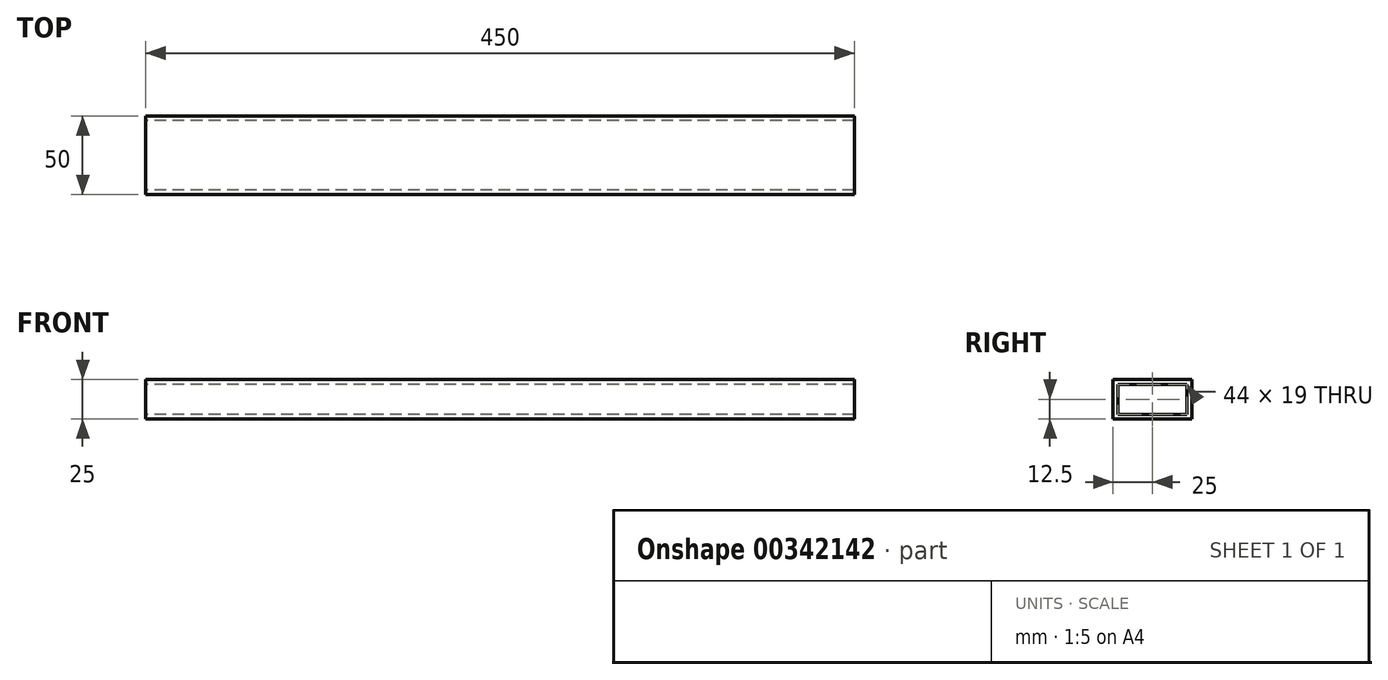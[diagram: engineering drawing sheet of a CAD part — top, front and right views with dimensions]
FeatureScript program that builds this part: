
annotation { "Feature Type Name" : "Feature", "Feature Type Description" : "" }
export const myFeature = defineFeature(function(context is Context, id is Id, definition is map)
    precondition{}
    {
        {
            var Q0;
            Q0=qCreatedBy(makeId("Right.planeOp"),FACE);
            var sketch = newSketch(context, id + "F0", { "sketchPlane" : qUnion([Q0])});
            skLineSegment(sketch, "E0.bottom", {"start": v(-25, 12.5) * mm, "end": v(25, 12.5) * mm});
            skLineSegment(sketch, "E0.top", {"start": v(-25, -12.5) * mm, "end": v(25, -12.5) * mm});
            skLineSegment(sketch, "E0.left", {"start": v(-25, 12.5) * mm, "end": v(-25, -12.5) * mm});
            skLineSegment(sketch, "E0.right", {"start": v(25, 12.5) * mm, "end": v(25, -12.5) * mm});
            skPoint(sketch, "E0.middle", {"position": v(0, 0) * mm});
            skLineSegment(sketch, "E1.bottom", {"start": v(-22, 9.5) * mm, "end": v(22, 9.5) * mm});
            skLineSegment(sketch, "E1.top", {"start": v(-22, -9.5) * mm, "end": v(22, -9.5) * mm});
            skLineSegment(sketch, "E1.left", {"start": v(-22, 9.5) * mm, "end": v(-22, -9.5) * mm});
            skLineSegment(sketch, "E1.right", {"start": v(22, 9.5) * mm, "end": v(22, -9.5) * mm});
            skSolve(sketch);
        }
        {
            var Q0;
            Q0=qSketchRegion(id+"F0",true);
            extrude(context, id + "F1", {"entities" : qUnion([Q0]), "endBound" : BoundingType.SYMMETRIC, "depth" : 450 * mm});
        }
    });
